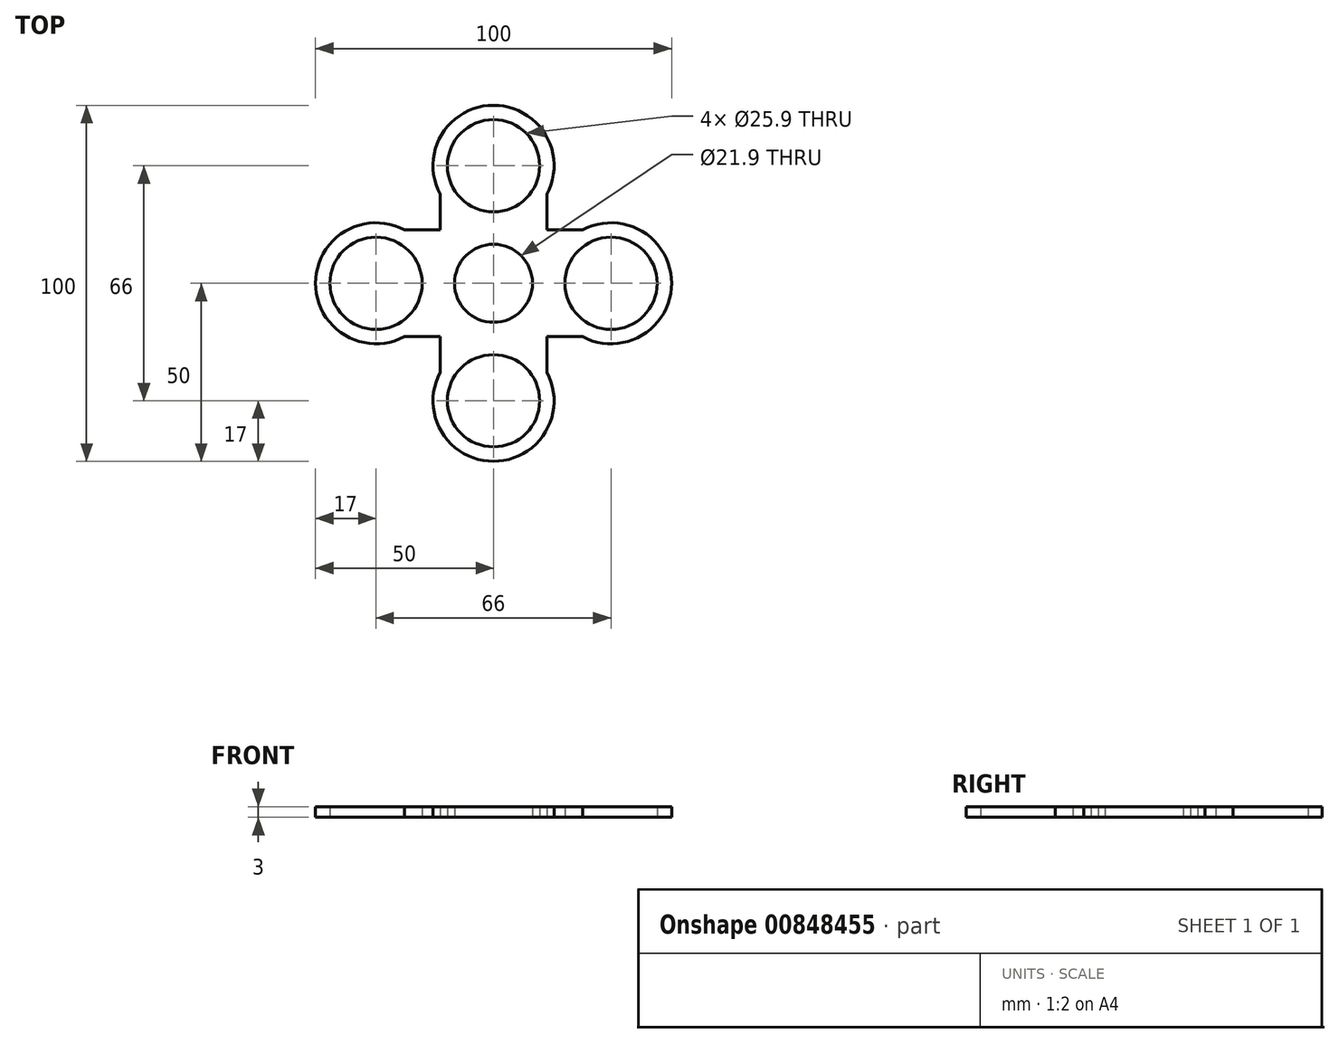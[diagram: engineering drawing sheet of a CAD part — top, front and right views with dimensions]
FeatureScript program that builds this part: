
annotation { "Feature Type Name" : "Feature", "Feature Type Description" : "" }
export const myFeature = defineFeature(function(context is Context, id is Id, definition is map)
    precondition{}
    {
        {
            var Q0;
            Q0=qCreatedBy(makeId("Top.planeOp"),FACE);
            var sketch = newSketch(context, id + "F0", { "sketchPlane" : qUnion([Q0])});
            skArc(sketch, "E0", {"start": v(-7.74, 7.74) * mm, "mid": v(-10.95, 0) * mm, "end": v(-7.74, -7.74) * mm});
            skCircle(sketch, "E1", {"center": v(-33, 0) * mm, "radius": 12.95 * mm});
            skArc(sketch, "E2", {"start": v(-25, 15) * mm, "mid": v(-50, 0) * mm, "end": v(-25, -15) * mm});
            skArc(sketch, "E3.1.1", {"start": v(-7.74, -7.74) * mm, "mid": v(0, -10.95) * mm, "end": v(7.74, -7.74) * mm});
            skArc(sketch, "E3.1.3", {"start": v(-15, -25) * mm, "mid": v(0, -50) * mm, "end": v(15, -25) * mm});
            skCircle(sketch, "E3.1.4", {"center": v(0, -33) * mm, "radius": 12.95 * mm});
            skArc(sketch, "E3.2.1", {"start": v(7.74, -7.74) * mm, "mid": v(10.95, 0) * mm, "end": v(7.74, 7.74) * mm});
            skArc(sketch, "E3.2.3", {"start": v(25, -15) * mm, "mid": v(50, 0) * mm, "end": v(25, 15) * mm});
            skCircle(sketch, "E3.2.4", {"center": v(33, 0) * mm, "radius": 12.95 * mm});
            skArc(sketch, "E3.3.1", {"start": v(7.74, 7.74) * mm, "mid": v(0, 10.95) * mm, "end": v(-7.74, 7.74) * mm});
            skArc(sketch, "E3.3.3", {"start": v(15, 25) * mm, "mid": v(0, 50) * mm, "end": v(-15, 25) * mm});
            skCircle(sketch, "E3.3.4", {"center": v(0, 33) * mm, "radius": 12.95 * mm});
            skLineSegment(sketch, "E4", {"start": v(-15, 15) * mm, "end": v(-25, 15) * mm});
            skLineSegment(sketch, "E5", {"start": v(15, 15) * mm, "end": v(25, 15) * mm});
            skLineSegment(sketch, "E6", {"start": v(-15, 15) * mm, "end": v(-15, 25) * mm});
            skLineSegment(sketch, "E7", {"start": v(-15, -15) * mm, "end": v(-15, -25) * mm});
            skLineSegment(sketch, "E8", {"start": v(15, 15) * mm, "end": v(15, 25) * mm});
            skLineSegment(sketch, "E9", {"start": v(15, -15) * mm, "end": v(15, -25) * mm});
            skLineSegment(sketch, "E10", {"start": v(-15, -15) * mm, "end": v(-25, -15) * mm});
            skLineSegment(sketch, "E11", {"start": v(-25, -15) * mm, "end": v(-15, -15) * mm});
            skLineSegment(sketch, "E12", {"start": v(15, -15) * mm, "end": v(25, -15) * mm});
            skSolve(sketch);
        }
        {
            var Q0;
            Q0 = qSketchRegion(id + "F0", true);
            extrude(context, id + "F1", {"entities" : qUnion([Q0]), "depth" : 3 * mm, "offsetDistance" : 25 * mm});
        }
    });
